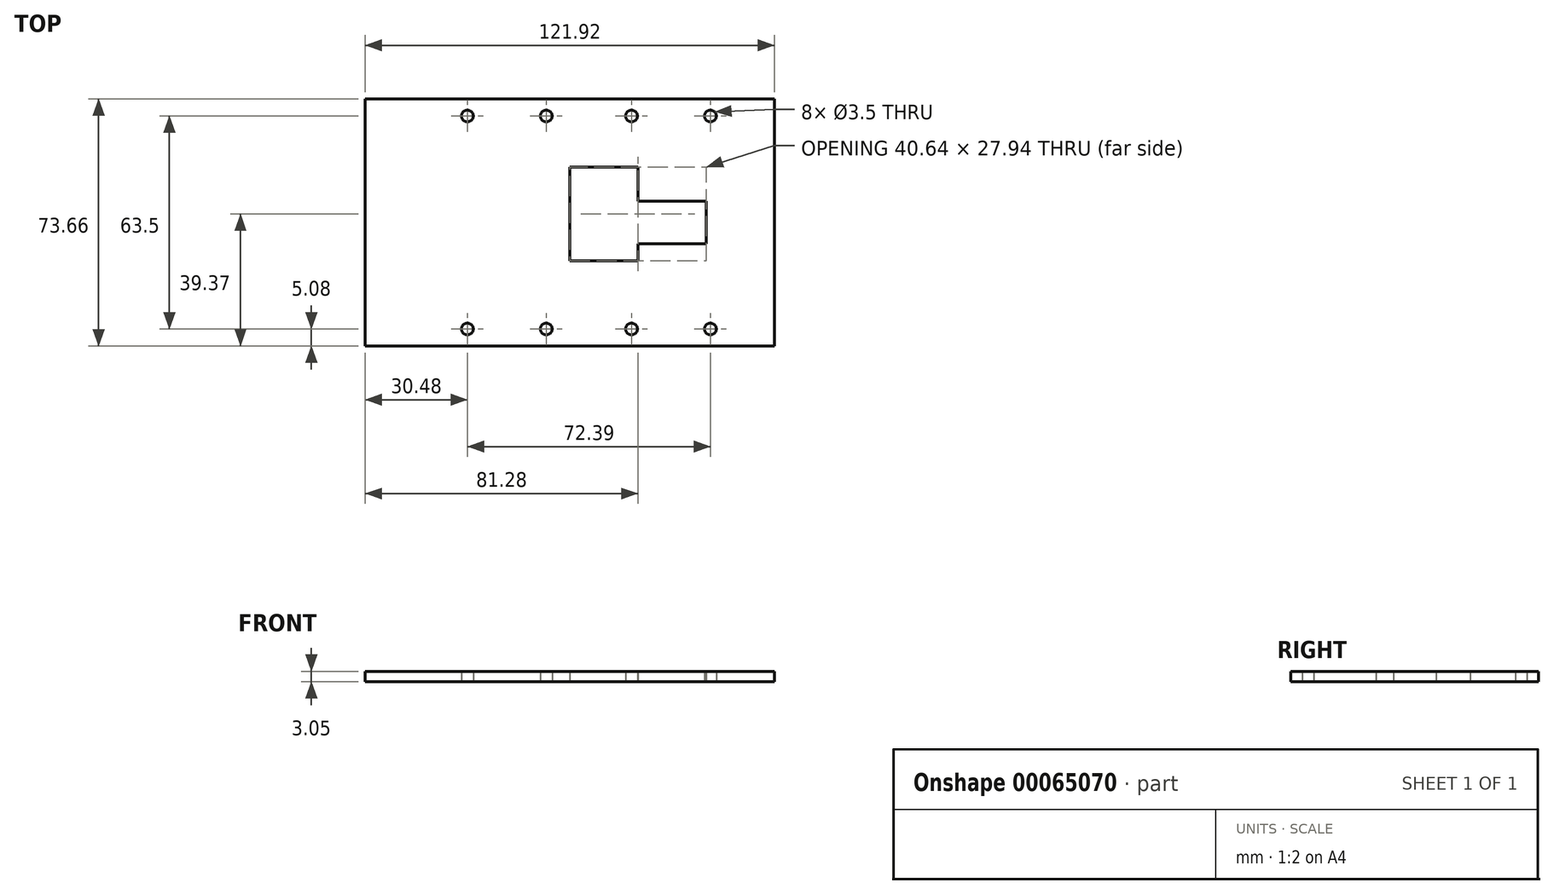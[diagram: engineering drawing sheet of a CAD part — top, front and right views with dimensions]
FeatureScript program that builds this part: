
annotation { "Feature Type Name" : "Feature", "Feature Type Description" : "" }
export const myFeature = defineFeature(function(context is Context, id is Id, definition is map)
    precondition{}
    {
        {
            var Q0;
            Q0=qCreatedBy(makeId("Top.planeOp"),FACE);
            var sketch = newSketch(context, id + "F0", { "sketchPlane" : qUnion([Q0])});
            skLineSegment(sketch, "E0.bottom", {"start": v(0, 0) * mm, "end": v(121.92, 0) * mm});
            skLineSegment(sketch, "E0.top", {"start": v(0, 73.66) * mm, "end": v(121.92, 73.66) * mm});
            skLineSegment(sketch, "E0.left", {"start": v(0, 0) * mm, "end": v(0, 73.66) * mm});
            skLineSegment(sketch, "E0.right", {"start": v(121.92, 0) * mm, "end": v(121.92, 73.66) * mm});
            skPoint(sketch, "E1", {"position": v(60.96, 25.4) * mm});
            skLineSegment(sketch, "E2.bottom", {"start": v(60.96, 25.4) * mm, "end": v(81.28, 25.4) * mm});
            skLineSegment(sketch, "E2.top", {"start": v(60.96, 53.34) * mm, "end": v(81.28, 53.34) * mm});
            skLineSegment(sketch, "E2.left", {"start": v(60.96, 25.4) * mm, "end": v(60.96, 53.34) * mm});
            skLineSegment(sketch, "E2.right", {"start": v(81.28, 43.18) * mm, "end": v(81.28, 53.34) * mm});
            skLineSegment(sketch, "E3.top", {"start": v(81.28, 43.18) * mm, "end": v(101.6, 43.18) * mm});
            skLineSegment(sketch, "E3.right", {"start": v(101.6, 30.48) * mm, "end": v(101.6, 43.18) * mm});
            skLineSegment(sketch, "E4", {"start": v(0, 5.08) * mm, "end": v(121.92, 5.08) * mm, "construction": true});
            skPoint(sketch, "E5", {"position": v(0, 36.83) * mm});
            skLineSegment(sketch, "E6", {"start": v(0, 36.83) * mm, "end": v(121.92, 36.83) * mm, "construction": true});
            skCircle(sketch, "E7", {"center": v(30.48, 5.08) * mm, "radius": 1.75 * mm});
            skCircle(sketch, "E8", {"center": v(53.98, 5.08) * mm, "radius": 1.75 * mm});
            skCircle(sketch, "E9", {"center": v(79.38, 5.08) * mm, "radius": 1.75 * mm});
            skCircle(sketch, "E10", {"center": v(102.87, 5.08) * mm, "radius": 1.75 * mm});
            skCircle(sketch, "E11.MirrorC", {"center": v(30.48, 68.58) * mm, "radius": 1.75 * mm});
            skCircle(sketch, "E12.MirrorC", {"center": v(53.98, 68.58) * mm, "radius": 1.75 * mm});
            skCircle(sketch, "E13.MirrorC", {"center": v(79.38, 68.58) * mm, "radius": 1.75 * mm});
            skCircle(sketch, "E14.MirrorC", {"center": v(102.87, 68.58) * mm, "radius": 1.75 * mm});
            skLineSegment(sketch, "E15", {"start": v(81.28, 30.48) * mm, "end": v(101.6, 30.48) * mm});
            skLineSegment(sketch, "E16.trimOffspring", {"start": v(81.28, 30.48) * mm, "end": v(81.28, 25.4) * mm});
            skSolve(sketch);
        }
        {
            var Q0;
            Q0=makeQuery(id+"F0.imprint","IMPRINT",FACE,{"disambiguationData":[TD([[makeQuery(id+"F0.imprint","IMPRINT",EDGE,{"derivedFrom":sQuery(id+"F0.wireOp",EDGE,"E0.bottom")}),1.0]])]});
            extrude(context, id + "F1", {"entities" : qUnion([Q0]), "depth" : 3.05 * mm, "offsetDistance" : 25.4 * mm});
        }
    });
